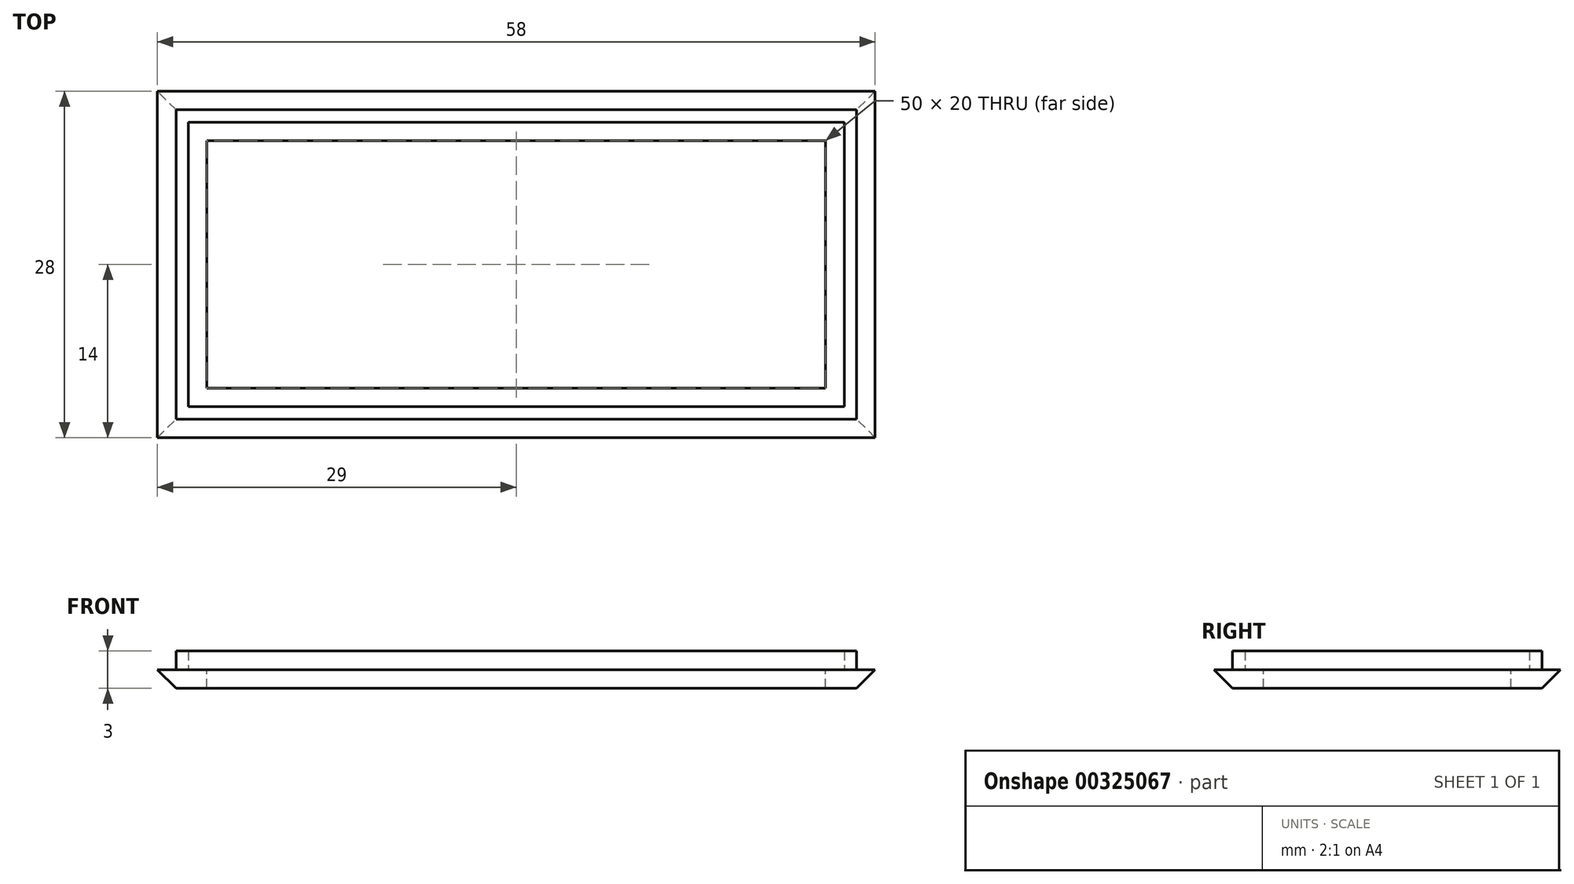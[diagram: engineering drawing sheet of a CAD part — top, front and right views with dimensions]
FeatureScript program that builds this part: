
annotation { "Feature Type Name" : "Feature", "Feature Type Description" : "" }
export const myFeature = defineFeature(function(context is Context, id is Id, definition is map)
    precondition{}
    {
        {
            var Q0;
            Q0=qCreatedBy(makeId("Top.planeOp"),FACE);
            var sketch = newSketch(context, id + "F0", { "sketchPlane" : qUnion([Q0])});
            skLineSegment(sketch, "E0.bottom", {"start": v(-29, 14) * mm, "end": v(29, 14) * mm});
            skLineSegment(sketch, "E0.top", {"start": v(-29, -14) * mm, "end": v(29, -14) * mm});
            skLineSegment(sketch, "E0.left", {"start": v(-29, 14) * mm, "end": v(-29, -14) * mm});
            skLineSegment(sketch, "E0.right", {"start": v(29, 14) * mm, "end": v(29, -14) * mm});
            skPoint(sketch, "E0.middle", {"position": v(0, 0) * mm});
            skLineSegment(sketch, "E1.0", {"start": v(-27.5, 12.5) * mm, "end": v(27.5, 12.5) * mm});
            skLineSegment(sketch, "E1.1", {"start": v(-27.5, 12.5) * mm, "end": v(-27.5, -12.5) * mm});
            skLineSegment(sketch, "E1.2", {"start": v(-27.5, -12.5) * mm, "end": v(27.5, -12.5) * mm});
            skLineSegment(sketch, "E1.3", {"start": v(27.5, 12.5) * mm, "end": v(27.5, -12.5) * mm});
            skLineSegment(sketch, "E2.0", {"start": v(-26.5, 11.5) * mm, "end": v(26.5, 11.5) * mm});
            skLineSegment(sketch, "E2.1", {"start": v(-26.5, 11.5) * mm, "end": v(-26.5, -11.5) * mm});
            skLineSegment(sketch, "E2.2", {"start": v(-26.5, -11.5) * mm, "end": v(26.5, -11.5) * mm});
            skLineSegment(sketch, "E2.3", {"start": v(26.5, 11.5) * mm, "end": v(26.5, -11.5) * mm});
            skLineSegment(sketch, "E3.0", {"start": v(-25, 10) * mm, "end": v(25, 10) * mm});
            skLineSegment(sketch, "E3.1", {"start": v(-25, 10) * mm, "end": v(-25, -10) * mm});
            skLineSegment(sketch, "E3.2", {"start": v(-25, -10) * mm, "end": v(25, -10) * mm});
            skLineSegment(sketch, "E3.3", {"start": v(25, 10) * mm, "end": v(25, -10) * mm});
            skSolve(sketch);
        }
        {
            var Q0;
            Q0 = qSketchRegion(id + "F0", true);
            var Q1;
            Q1=makeQuery(id+"F0.imprint","IMPRINT",FACE,{"disambiguationData":[TD([[makeQuery(id+"F0.imprint","IMPRINT",EDGE,{"derivedFrom":sQuery(id+"F0.wireOp",EDGE,"E1.0")}),-1.0]])]});
            var Q2;
            Q2=makeQuery(id+"F0.imprint","IMPRINT",FACE,{"disambiguationData":[TD([[makeQuery(id+"F0.imprint","IMPRINT",EDGE,{"derivedFrom":sQuery(id+"F0.wireOp",EDGE,"E2.0")}),-1.0]])]});
            extrude(context, id + "F1", {"entities" : qUnion([Q0, Q1, Q2]), "oppositeDirection" : true, "depth" : 1.5 * mm, "offsetDistance" : 25 * mm});
        }
        {
            var Q0;
            Q0=makeQuery(id+"F0.imprint","IMPRINT",FACE,{"disambiguationData":[TD([[makeQuery(id+"F0.imprint","IMPRINT",EDGE,{"derivedFrom":sQuery(id+"F0.wireOp",EDGE,"E1.0")}),-1.0]])]});
            extrude(context, id + "F2", {"entities" : qUnion([Q0]), "operationType" : NewBodyOperationType.ADD, "depth" : 1.5 * mm, "offsetDistance" : 25 * mm});
        }
        {
            var Q0;
            Q0=makeQuery(id+"F1.opExtrude","CAP_EDGE",EDGE,{"disambiguationData":[OSD([sQuery(id+"F0.wireOp",EDGE,"E0.top")])],"isStart":false});
            var Q1;
            Q1=makeQuery(id+"F1.opExtrude","CAP_EDGE",EDGE,{"disambiguationData":[OSD([sQuery(id+"F0.wireOp",EDGE,"E0.left")])],"isStart":false});
            var Q2;
            Q2=makeQuery(id+"F1.opExtrude","CAP_EDGE",EDGE,{"disambiguationData":[OSD([sQuery(id+"F0.wireOp",EDGE,"E0.bottom")])],"isStart":false});
            var Q3;
            Q3=makeQuery(id+"F1.opExtrude","CAP_EDGE",EDGE,{"disambiguationData":[OSD([sQuery(id+"F0.wireOp",EDGE,"E0.right")])],"isStart":false});
            chamfer(context, id + "F3", {"entities" : qUnion([Q0, Q1, Q2, Q3]), "width" : 1.5 * mm, "tangentPropagation" : true});
        }
    });
